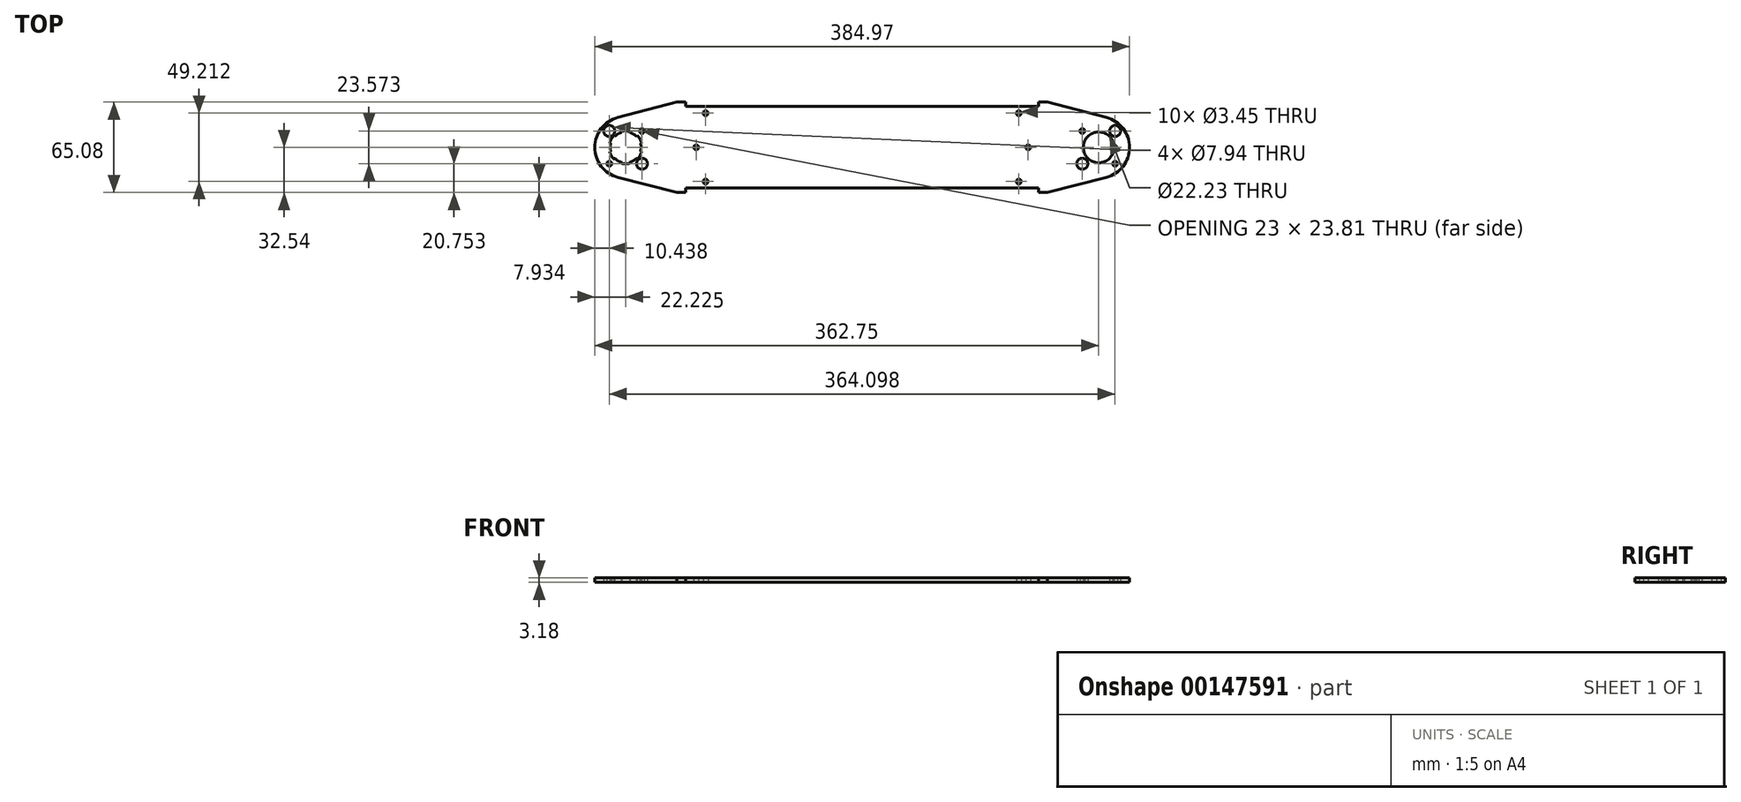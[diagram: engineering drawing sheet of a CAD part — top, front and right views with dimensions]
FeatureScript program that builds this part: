
annotation { "Feature Type Name" : "Feature", "Feature Type Description" : "" }
export const myFeature = defineFeature(function(context is Context, id is Id, definition is map)
    precondition{}
    {
        {
            var Q0;
            Q0=qCreatedBy(makeId("Top.planeOp"),FACE);
            var sketch = newSketch(context, id + "F0", { "sketchPlane" : qUnion([Q0])});
            skPoint(sketch, "E0.rect.middle", {"position": v(0, 0) * mm});
            skCircle(sketch, "E1", {"center": v(0, 0) * mm, "radius": 11.11 * mm});
            skLineSegment(sketch, "E2.bottom", {"start": v(11.79, 11.79) * mm, "end": v(-11.79, 11.79) * mm, "construction": true});
            skLineSegment(sketch, "E2.left", {"start": v(11.79, 11.79) * mm, "end": v(11.79, -11.79) * mm, "construction": true});
            skLineSegment(sketch, "E2.right", {"start": v(-11.79, 11.79) * mm, "end": v(-11.79, -11.79) * mm, "construction": true});
            skCircle(sketch, "E3", {"center": v(-11.79, 11.79) * mm, "radius": 1.73 * mm});
            skCircle(sketch, "E4", {"center": v(11.79, 11.79) * mm, "radius": 3.97 * mm});
            skCircle(sketch, "E5", {"center": v(11.79, -11.79) * mm, "radius": 1.73 * mm});
            skCircle(sketch, "E6", {"center": v(-11.79, -11.79) * mm, "radius": 3.97 * mm});
            skArc(sketch, "E7", {"start": v(-346.1, 21.51) * mm, "mid": v(-362.75, 0) * mm, "end": v(-346.1, -21.51) * mm});
            skLineSegment(sketch, "E8.bottom", {"start": v(-352.31, 11.79) * mm, "end": v(-328.74, 11.79) * mm, "construction": true});
            skLineSegment(sketch, "E8.top", {"start": v(-352.31, -11.79) * mm, "end": v(-328.74, -11.79) * mm, "construction": true});
            skLineSegment(sketch, "E8.left", {"start": v(-352.31, 11.79) * mm, "end": v(-352.31, -11.79) * mm, "construction": true});
            skLineSegment(sketch, "E8.right", {"start": v(-328.74, 11.79) * mm, "end": v(-328.74, -11.79) * mm, "construction": true});
            skCircle(sketch, "E9", {"center": v(-328.74, 11.79) * mm, "radius": 1.73 * mm});
            skCircle(sketch, "E10", {"center": v(-340.53, 0) * mm, "radius": 11.11 * mm});
            skCircle(sketch, "E11", {"center": v(-352.31, 11.79) * mm, "radius": 3.97 * mm});
            skCircle(sketch, "E12", {"center": v(-352.31, -11.79) * mm, "radius": 1.73 * mm});
            skCircle(sketch, "E13", {"center": v(-328.74, -11.79) * mm, "radius": 3.97 * mm});
            skLineSegment(sketch, "E14", {"start": v(0, 0) * mm, "end": v(-340.53, 0) * mm, "construction": true});
            skLineSegment(sketch, "E15", {"start": v(-346.1, -21.51) * mm, "end": v(-303.61, -32.54) * mm});
            skLineSegment(sketch, "E16", {"start": v(-346.1, 21.51) * mm, "end": v(-303.61, 32.54) * mm});
            skLineSegment(sketch, "E17", {"start": v(-297.26, -29.37) * mm, "end": v(-43.26, -29.37) * mm});
            skLineSegment(sketch, "E18", {"start": v(-297.26, 29.37) * mm, "end": v(-43.26, 29.37) * mm});
            skLineSegment(sketch, "E19", {"start": v(-297.26, 32.54) * mm, "end": v(-297.26, 29.37) * mm});
            skLineSegment(sketch, "E20", {"start": v(-297.26, 32.54) * mm, "end": v(-303.61, 32.54) * mm});
            skLineSegment(sketch, "E21", {"start": v(-297.26, -29.37) * mm, "end": v(-297.26, -32.54) * mm});
            skLineSegment(sketch, "E22", {"start": v(-297.26, -32.54) * mm, "end": v(-303.61, -32.54) * mm});
            skLineSegment(sketch, "E23", {"start": v(-43.26, -29.37) * mm, "end": v(-43.26, -32.54) * mm});
            skLineSegment(sketch, "E24", {"start": v(-43.26, -32.54) * mm, "end": v(-36.91, -32.54) * mm});
            skLineSegment(sketch, "E25", {"start": v(-43.26, 29.37) * mm, "end": v(-43.26, 32.54) * mm});
            skLineSegment(sketch, "E26", {"start": v(-43.26, 32.54) * mm, "end": v(-36.91, 32.54) * mm});
            skLineSegment(sketch, "E27", {"start": v(-36.91, -32.54) * mm, "end": v(5.58, -21.51) * mm});
            skLineSegment(sketch, "E28", {"start": v(5.58, 21.51) * mm, "end": v(-36.91, 32.54) * mm});
            skLineSegment(sketch, "E29", {"start": v(-297.26, 29.37) * mm, "end": v(-297.26, 24.6) * mm, "construction": true});
            skLineSegment(sketch, "E30", {"start": v(-297.26, 24.6) * mm, "end": v(-282.98, 24.6) * mm, "construction": true});
            skLineSegment(sketch, "E31", {"start": v(-297.26, -29.37) * mm, "end": v(-297.26, -24.6) * mm, "construction": true});
            skLineSegment(sketch, "E32", {"start": v(-297.26, -24.6) * mm, "end": v(-282.98, -24.6) * mm, "construction": true});
            skLineSegment(sketch, "E33", {"start": v(-43.26, -29.37) * mm, "end": v(-43.26, -24.6) * mm, "construction": true});
            skLineSegment(sketch, "E34", {"start": v(-43.26, -24.6) * mm, "end": v(-57.55, -24.6) * mm, "construction": true});
            skLineSegment(sketch, "E35", {"start": v(-43.26, 29.37) * mm, "end": v(-43.26, 24.6) * mm, "construction": true});
            skLineSegment(sketch, "E36", {"start": v(-43.26, 24.6) * mm, "end": v(-57.55, 24.6) * mm, "construction": true});
            skCircle(sketch, "E37", {"center": v(-282.98, 24.6) * mm, "radius": 1.73 * mm});
            skCircle(sketch, "E38", {"center": v(-57.55, 24.6) * mm, "radius": 1.73 * mm});
            skCircle(sketch, "E39", {"center": v(-57.55, -24.6) * mm, "radius": 1.73 * mm});
            skCircle(sketch, "E40", {"center": v(-282.98, -24.6) * mm, "radius": 1.73 * mm});
            skLineSegment(sketch, "E41", {"start": v(-11.79, -11.79) * mm, "end": v(11.79, -11.79) * mm, "construction": true});
            skLineSegment(sketch, "E42", {"start": v(-170.26, -29.37) * mm, "end": v(-170.26, 0) * mm, "construction": true});
            skLineSegment(sketch, "E43", {"start": v(-170.26, 0) * mm, "end": v(-170.26, 29.37) * mm, "construction": true});
            skArc(sketch, "E44", {"start": v(5.58, -21.51) * mm, "mid": v(22.23, 0) * mm, "end": v(5.58, 21.51) * mm});
            skLineSegment(sketch, "E45", {"start": v(-328.74, 11.79) * mm, "end": v(-289.73, 11.79) * mm, "construction": true});
            skLineSegment(sketch, "E46", {"start": v(-289.73, 11.79) * mm, "end": v(-289.73, 0) * mm, "construction": true});
            skLineSegment(sketch, "E47", {"start": v(-11.79, 11.79) * mm, "end": v(-50.8, 11.79) * mm, "construction": true});
            skLineSegment(sketch, "E48", {"start": v(-50.8, 11.79) * mm, "end": v(-50.8, 0) * mm, "construction": true});
            skCircle(sketch, "E49", {"center": v(-289.73, 0) * mm, "radius": 1.73 * mm});
            skCircle(sketch, "E50", {"center": v(-50.8, 0) * mm, "radius": 1.73 * mm});
            skCircle(sketch, "E51", {"center": v(11.79, 11.79) * mm, "radius": 5.56 * mm, "construction": true});
            skSolve(sketch);
        }
        {
            var Q0;
            Q0=qSketchRegion(id+"F0",true);
            extrude(context, id + "F1", {"entities" : qUnion([Q0]), "depth" : 3.17 * mm});
        }
        {
            var Q0;
            Q0=makeQuery(id+"F1.opExtrude","CAP_FACE",FACE,{"disambiguationData":[OSD([sQuery(id+"F0.wireOp",EDGE,"d63eafa0-1946-4b0e-8293-95e246b273c5.rect.bottom"),sQuery(id+"F0.wireOp",EDGE,"d63eafa0-1946-4b0e-8293-95e246b273c5.rect.top"),sQuery(id+"F0.wireOp",EDGE,"5983dcdd-59a7-4b72-80fd-e4567be1ae8a"),sQuery(id+"F0.wireOp",EDGE,"5a538b3e-fc2b-4d64-affd-5d60433388e5"),sQuery(id+"F0.wireOp",EDGE,"72e86de7-b207-474f-aadf-64543fae3f9b"),sQuery(id+"F0.wireOp",EDGE,"1c038800-5bd5-4753-8b38-6da13ef78ef9"),sQuery(id+"F0.wireOp",EDGE,"EbMUZoU6-Ffds-1dNq-SxhE-hPi8oSjhvaod"),sQuery(id+"F0.wireOp",EDGE,"RfgQjzcw-1Izs-lnTa-bWkk-oBHRDQjbZqQC"),sQuery(id+"F0.wireOp",EDGE,"1cCQAcjj-TyQA-3DMx-kDix-v5yZVaaGeXVM"),sQuery(id+"F0.wireOp",EDGE,"7KPu8lni-3ZWA-t6oJ-FRoh-C5MB3aVr7E9B"),sQuery(id+"F0.wireOp",EDGE,"bSzr06ES-7M0i-Fw5H-UJmt-4e4EQGRPIe4n"),sQuery(id+"F0.wireOp",EDGE,"WGsr6OjU-OX8l-mawA-7cCc-MfOuMOY06Cp5"),sQuery(id+"F0.wireOp",EDGE,"9mrz1cDN-18gM-20ra-6VCO-jp25g10tvNn2"),sQuery(id+"F0.wireOp",EDGE,"G0uOisy3-Mq6h-PcKh-Zkf4-CVoCvP3Hii1l"),sQuery(id+"F0.wireOp",EDGE,"1ae556be-0ab9-4322-b48e-98cf5a741ae0"),sQuery(id+"F0.wireOp",EDGE,"676cd913-43f8-42b3-8cdc-a90136d19ef5"),sQuery(id+"F0.wireOp",EDGE,"xnt2EyF8-ZVyQ-RbWD-GIsP-ThkcyX8ZioIH.bottom"),sQuery(id+"F0.wireOp",EDGE,"xnt2EyF8-ZVyQ-RbWD-GIsP-ThkcyX8ZioIH.top"),sQuery(id+"F0.wireOp",EDGE,"xnt2EyF8-ZVyQ-RbWD-GIsP-ThkcyX8ZioIH.left"),sQuery(id+"F0.wireOp",EDGE,"E1"),sQuery(id+"F0.wireOp",EDGE,"Jo9pZc7T-t0kF-vjz1-dNbX-L65bwNqtrrdz"),sQuery(id+"F0.wireOp",EDGE,"lEYoY9t7-PMOS-SVp6-xfnB-Xp9WdWMCDdum"),sQuery(id+"F0.wireOp",EDGE,"s7aM02SC-9XQ7-dueL-DqMg-ZFuJqOofj9mt"),sQuery(id+"F0.wireOp",EDGE,"deKa9ngt-XMq2-GGkr-SZIa-KlyN0U5bcCDe"),sQuery(id+"F0.wireOp",EDGE,"E3"),sQuery(id+"F0.wireOp",EDGE,"E4"),sQuery(id+"F0.wireOp",EDGE,"E5"),sQuery(id+"F0.wireOp",EDGE,"E6"),sQuery(id+"F0.wireOp",EDGE,"E7"),sQuery(id+"F0.wireOp",EDGE,"E9"),sQuery(id+"F0.wireOp",EDGE,"E10"),sQuery(id+"F0.wireOp",EDGE,"E11"),sQuery(id+"F0.wireOp",EDGE,"E12"),sQuery(id+"F0.wireOp",EDGE,"E13")])],"isStart":true});
            var sketch = newSketch(context, id + "F2", { "sketchPlane" : qUnion([Q0])});
            skLineSegment(sketch, "E52", {"start": v(-340.53, 0) * mm, "end": v(-350.15, -5.56) * mm, "construction": true});
            skArc(sketch, "E53", {"start": v(-351.26, -2.88) * mm, "mid": v(-350.15, -5.56) * mm, "end": v(-348.38, -7.86) * mm});
            skLineSegment(sketch, "E54", {"start": v(-340.53, 0) * mm, "end": v(-348.38, -7.86) * mm, "construction": true});
            skLineSegment(sketch, "E55", {"start": v(-340.53, 0) * mm, "end": v(-351.26, -2.88) * mm, "construction": true});
            skLineSegment(sketch, "E56", {"start": v(-348.38, -7.86) * mm, "end": v(-348.94, -8.42) * mm});
            skLineSegment(sketch, "E57", {"start": v(-351.26, -2.88) * mm, "end": v(-352.03, -3.08) * mm});
            skArc(sketch, "E58", {"start": v(-352.03, -3.08) * mm, "mid": v(-350.84, -5.95) * mm, "end": v(-348.94, -8.42) * mm});
            skLineSegment(sketch, "E59", {"start": v(-340.53, 0) * mm, "end": v(-351.64, 0) * mm, "construction": true});
            skSolve(sketch);
        }
        {
            var Q0;
            Q0=qSketchRegion(id+"F2",true);
            var Q1;
            Q1=makeQuery(id+"F1.opExtrude","CAP_FACE",FACE,{"disambiguationData":[OSD([sQuery(id+"F0.wireOp",EDGE,"d63eafa0-1946-4b0e-8293-95e246b273c5.rect.bottom"),sQuery(id+"F0.wireOp",EDGE,"d63eafa0-1946-4b0e-8293-95e246b273c5.rect.top"),sQuery(id+"F0.wireOp",EDGE,"5983dcdd-59a7-4b72-80fd-e4567be1ae8a"),sQuery(id+"F0.wireOp",EDGE,"5a538b3e-fc2b-4d64-affd-5d60433388e5"),sQuery(id+"F0.wireOp",EDGE,"72e86de7-b207-474f-aadf-64543fae3f9b"),sQuery(id+"F0.wireOp",EDGE,"1c038800-5bd5-4753-8b38-6da13ef78ef9"),sQuery(id+"F0.wireOp",EDGE,"EbMUZoU6-Ffds-1dNq-SxhE-hPi8oSjhvaod"),sQuery(id+"F0.wireOp",EDGE,"RfgQjzcw-1Izs-lnTa-bWkk-oBHRDQjbZqQC"),sQuery(id+"F0.wireOp",EDGE,"1cCQAcjj-TyQA-3DMx-kDix-v5yZVaaGeXVM"),sQuery(id+"F0.wireOp",EDGE,"7KPu8lni-3ZWA-t6oJ-FRoh-C5MB3aVr7E9B"),sQuery(id+"F0.wireOp",EDGE,"bSzr06ES-7M0i-Fw5H-UJmt-4e4EQGRPIe4n"),sQuery(id+"F0.wireOp",EDGE,"WGsr6OjU-OX8l-mawA-7cCc-MfOuMOY06Cp5"),sQuery(id+"F0.wireOp",EDGE,"9mrz1cDN-18gM-20ra-6VCO-jp25g10tvNn2"),sQuery(id+"F0.wireOp",EDGE,"G0uOisy3-Mq6h-PcKh-Zkf4-CVoCvP3Hii1l"),sQuery(id+"F0.wireOp",EDGE,"1ae556be-0ab9-4322-b48e-98cf5a741ae0"),sQuery(id+"F0.wireOp",EDGE,"676cd913-43f8-42b3-8cdc-a90136d19ef5"),sQuery(id+"F0.wireOp",EDGE,"xnt2EyF8-ZVyQ-RbWD-GIsP-ThkcyX8ZioIH.bottom"),sQuery(id+"F0.wireOp",EDGE,"xnt2EyF8-ZVyQ-RbWD-GIsP-ThkcyX8ZioIH.top"),sQuery(id+"F0.wireOp",EDGE,"xnt2EyF8-ZVyQ-RbWD-GIsP-ThkcyX8ZioIH.left"),sQuery(id+"F0.wireOp",EDGE,"E1"),sQuery(id+"F0.wireOp",EDGE,"Jo9pZc7T-t0kF-vjz1-dNbX-L65bwNqtrrdz"),sQuery(id+"F0.wireOp",EDGE,"lEYoY9t7-PMOS-SVp6-xfnB-Xp9WdWMCDdum"),sQuery(id+"F0.wireOp",EDGE,"s7aM02SC-9XQ7-dueL-DqMg-ZFuJqOofj9mt"),sQuery(id+"F0.wireOp",EDGE,"deKa9ngt-XMq2-GGkr-SZIa-KlyN0U5bcCDe"),sQuery(id+"F0.wireOp",EDGE,"E3"),sQuery(id+"F0.wireOp",EDGE,"E4"),sQuery(id+"F0.wireOp",EDGE,"E5"),sQuery(id+"F0.wireOp",EDGE,"E6"),sQuery(id+"F0.wireOp",EDGE,"E7"),sQuery(id+"F0.wireOp",EDGE,"E9"),sQuery(id+"F0.wireOp",EDGE,"E10"),sQuery(id+"F0.wireOp",EDGE,"E11"),sQuery(id+"F0.wireOp",EDGE,"E12"),sQuery(id+"F0.wireOp",EDGE,"E13")])],"isStart":false});
            extrude(context, id + "F3", {"entities" : qUnion([Q0]), "operationType" : NewBodyOperationType.REMOVE, "endBound" : BoundingType.UP_TO_SURFACE, "oppositeDirection" : true, "endBoundEntityFace" : qUnion([Q1]), "depth" : 25.4 * mm});
        }
        {
            var Q0;
            Q0=makeQuery(id+"F3.boolean.opBoolean","COPY",FACE,{"derivedFrom":makeQuery(id+"F3.opExtrude","SWEPT_FACE",FACE,{"disambiguationData":[OSD([sQuery(id+"F2.wireOp",EDGE,"E56")])]})});
            var Q1;
            Q1=makeQuery(id+"F3.boolean.opBoolean","COPY",FACE,{"derivedFrom":makeQuery(id+"F3.opExtrude","SWEPT_FACE",FACE,{"disambiguationData":[OSD([sQuery(id+"F2.wireOp",EDGE,"E58")])]})});
            var Q2;
            Q2=makeQuery(id+"F3.boolean.opBoolean","COPY",FACE,{"derivedFrom":makeQuery(id+"F3.opExtrude","SWEPT_FACE",FACE,{"disambiguationData":[OSD([sQuery(id+"F2.wireOp",EDGE,"E57")])]})});
            var Q3;
            Q3=makeQuery(id+"F1.opExtrude","SWEPT_FACE",FACE,{"disambiguationData":[OSD([sQuery(id+"F0.wireOp",EDGE,"E10")])]});
            circularPattern(context, id + "F4", {"patternType" : PatternType.FACE, "faces" : qUnion([Q0, Q1, Q2]), "axis" : qUnion([Q3]), "angle" : 60 * degree, "instanceCount" : 6});
        }
    });
